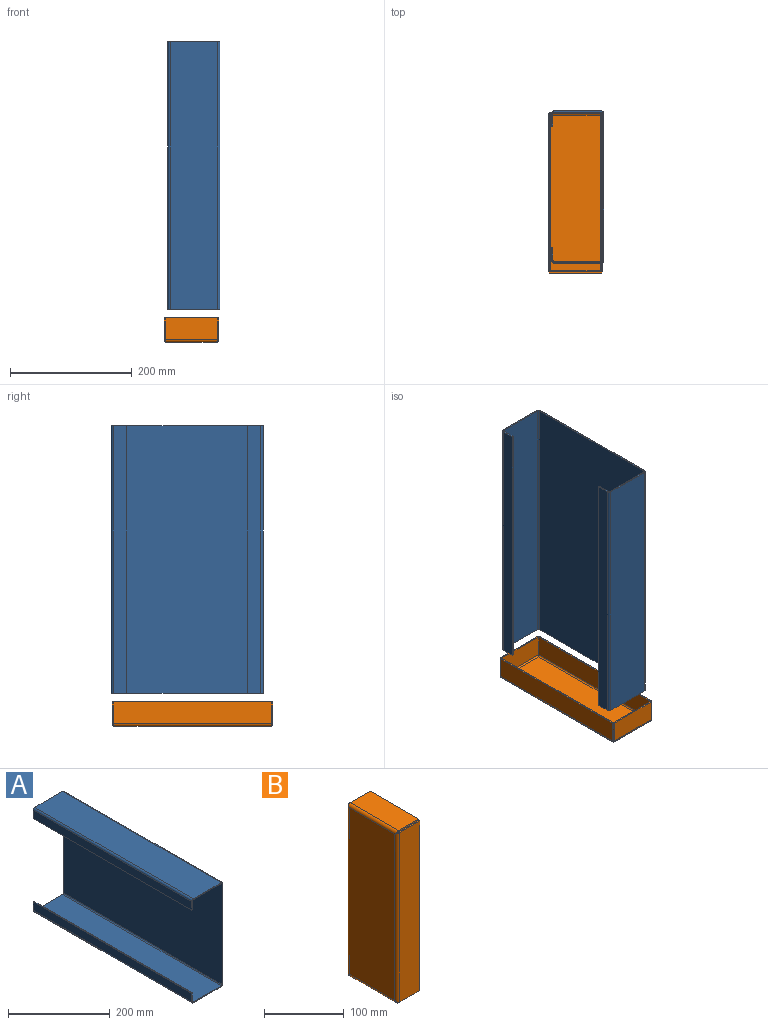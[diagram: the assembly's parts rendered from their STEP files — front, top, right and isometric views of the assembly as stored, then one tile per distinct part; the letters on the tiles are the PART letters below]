
ASSEMBLY  parts=2 mates=2
PART A: 38 faces, bbox 86x440x250 mm
  f0: plane 20.7x2mm, normal (0,1,0), area 41.4mm2, adj f2,f3,f4,f35
  f1: plane 20.7x2mm, normal (0,-1,0), area 41.4mm2, adj f2,f3,f4,f34
  f2: plane 440x2mm, normal (0,0,-1), area 880mm2, adj f0,f1,f3,f4
  f3: plane 440x20.7mm, normal (1,0,0), area 9108mm2, adj f0,f1,f2,f37
  f4: plane 440x20.7mm, normal (-1,0,0), area 9108mm2, adj f0,f1,f2,f36
  f5: plane 77.4x2mm, normal (0,1,0), area 154.8mm2, adj f7,f8,f31,f35
  f6: plane 77.4x2mm, normal (0,-1,0), area 154.8mm2, adj f7,f8,f30,f34
  f7: plane 440x77.4mm, normal (0,0,-1), area 34056mm2, adj f5,f6,f33,f37
  f8: plane 440x77.4mm, normal (0,0,1), area 34056mm2, adj f5,f6,f32,f36
  f9: plane 241.4x2mm, normal (0,1,0), area 482.8mm2, adj f11,f12,f27,f31
  f10: plane 241.4x2mm, normal (0,-1,0), area 482.8mm2, adj f11,f12,f26,f30
  f11: plane 440x241.4mm, normal (-1,0,0), area 106216mm2, adj f9,f10,f29,f33
  f12: plane 440x241.4mm, normal (1,0,0), area 106216mm2, adj f9,f10,f28,f32
  f13: plane 77.4x2mm, normal (0,1,0), area 154.8mm2, adj f15,f16,f23,f27
  f14: plane 77.4x2mm, normal (0,-1,0), area 154.8mm2, adj f15,f16,f22,f26
  f15: plane 440x77.4mm, normal (0,0,1), area 34056mm2, adj f13,f14,f25,f29
  f16: plane 440x77.4mm, normal (0,0,-1), area 34056mm2, adj f13,f14,f24,f28
  f17: plane 20.7x2mm, normal (0,1,0), area 41.4mm2, adj f18,f20,f21,f23
  f18: plane 440x2mm, normal (0,0,1), area 880mm2, adj f17,f19,f20,f21
  f19: plane 20.7x2mm, normal (0,-1,0), area 41.4mm2, adj f18,f20,f21,f22
  f20: plane 440x20.7mm, normal (1,0,0), area 9108mm2, adj f17,f18,f19,f25
  f21: plane 440x20.7mm, normal (-1,0,0), area 9108mm2, adj f17,f18,f19,f24
  f22: plane 4.3x4.3mm, normal (0,-1,0), area 10.4mm2, adj f14,f19,f24,f25
  f23: plane 4.3x4.3mm, normal (0,1,0), area 10.4mm2, adj f13,f17,f24,f25
  f24: cylinder r=4.3mm len=440mm, axis (0,-1,0), area 2971.9mm2, adj f16,f21,f22,f23
  f25: cylinder r=2.3mm len=440mm, axis (0,-1,0), area 1589.6mm2, adj f15,f20,f22,f23
  f26: plane 4.3x4.3mm, normal (0,-1,0), area 10.4mm2, adj f10,f14,f28,f29
  f27: plane 4.3x4.3mm, normal (0,1,0), area 10.4mm2, adj f9,f13,f28,f29
  f28: cylinder r=4.3mm len=440mm, axis (0,-1,0), area 2971.9mm2, adj f12,f16,f26,f27
  f29: cylinder r=2.3mm len=440mm, axis (0,-1,0), area 1589.6mm2, adj f11,f15,f26,f27
  f30: plane 4.3x4.3mm, normal (0,-1,0), area 10.4mm2, adj f6,f10,f32,f33
  f31: plane 4.3x4.3mm, normal (0,1,0), area 10.4mm2, adj f5,f9,f32,f33
  f32: cylinder r=4.3mm len=440mm, axis (0,-1,0), area 2971.9mm2, adj f8,f12,f30,f31
  f33: cylinder r=2.3mm len=440mm, axis (0,-1,0), area 1589.6mm2, adj f7,f11,f30,f31
  f34: plane 4.3x4.3mm, normal (0,-1,0), area 10.4mm2, adj f1,f6,f36,f37
  f35: plane 4.3x4.3mm, normal (0,1,0), area 10.4mm2, adj f0,f5,f36,f37
  f36: cylinder r=4.3mm len=440mm, axis (0,-1,0), area 2971.9mm2, adj f4,f8,f34,f35
  f37: cylinder r=2.3mm len=440mm, axis (0,-1,0), area 1589.6mm2, adj f3,f7,f34,f35
PART B: 42 faces, bbox 40x90x264 mm
  f0: plane 255.4x81.4mm, normal (-1,0,0), area 20789.6mm2, adj f2,f3,f4,f5,f13,f22,f31,f40
  f1: plane 255.4x81.4mm, normal (1,0,0), area 20789.6mm2, adj f2,f3,f4,f5,f14,f23,f32,f41
  f2: plane 2x0.01mm, normal (0,-0.71,0.71), area 0mm2, adj f0,f1,f21,f29
  f3: plane 2x0.01mm, normal (0,0.71,0.71), area 0mm2, adj f0,f1,f20,f38
  f4: plane 2x0.01mm, normal (0,0.71,-0.71), area 0mm2, adj f0,f1,f11,f39
  f5: plane 2x0.01mm, normal (0,-0.71,-0.71), area 0mm2, adj f0,f1,f12,f30
  f6: plane 85.96x2mm, normal (1,0,0), area 171.9mm2, adj f7,f8,f9,f10
  f7: plane 35.7x2mm, normal (0,-1,0), area 71.4mm2, adj f6,f9,f10,f12
  f8: plane 35.7x2mm, normal (0,1,0), area 71.4mm2, adj f6,f9,f10,f11
  f9: plane 85.96x35.7mm, normal (0,0,-1), area 3068.8mm2, adj f6,f7,f8,f13
  f10: plane 85.96x35.7mm, normal (0,0,1), area 3068.8mm2, adj f6,f7,f8,f14
  f11: bspline ~4.3x4.3mm, area 11.6mm2, adj f4,f8,f13,f14
  f12: bspline ~4.3x4.3mm, area 11.5mm2, adj f5,f7,f13,f14
  f13: cylinder r=4.3mm len=85.96mm, axis (0,1,0), area 569.4mm2, adj f0,f9,f11,f12
  f14: cylinder r=2.3mm len=85.96mm, axis (0,1,0), area 304.6mm2, adj f1,f10,f11,f12
  f15: plane 85.96x2mm, normal (1,0,0), area 171.9mm2, adj f16,f17,f18,f19
  f16: plane 35.7x2mm, normal (0,1,0), area 71.4mm2, adj f15,f18,f19,f20
  f17: plane 35.7x2mm, normal (0,-1,0), area 71.4mm2, adj f15,f18,f19,f21
  f18: plane 85.96x35.7mm, normal (0,0,1), area 3068.8mm2, adj f15,f16,f17,f22
  f19: plane 85.96x35.7mm, normal (0,0,-1), area 3068.8mm2, adj f15,f16,f17,f23
  f20: bspline ~4.3x4.3mm, area 11.5mm2, adj f3,f16,f22,f23
  f21: bspline ~4.3x4.3mm, area 11.6mm2, adj f2,f17,f22,f23
  f22: cylinder r=4.3mm len=85.96mm, axis (0,1,0), area 569.4mm2, adj f0,f18,f20,f21
  f23: cylinder r=2.3mm len=85.96mm, axis (0,1,0), area 304.5mm2, adj f1,f19,f20,f21
  f24: plane 259.96x2mm, normal (1,0,0), area 519.9mm2, adj f25,f26,f27,f28
  f25: plane 35.7x2mm, normal (0,0,1), area 71.4mm2, adj f24,f27,f28,f29
  f26: plane 35.7x2mm, normal (0,0,-1), area 71.4mm2, adj f24,f27,f28,f30
  f27: plane 259.96x35.7mm, normal (0,-1,0), area 9280.6mm2, adj f24,f25,f26,f31
  f28: plane 259.96x35.7mm, normal (0,1,0), area 9280.6mm2, adj f24,f25,f26,f32
  f29: bspline ~4.3x4.3mm, area 11.5mm2, adj f2,f25,f31,f32
  f30: bspline ~4.3x4.3mm, area 11.6mm2, adj f5,f26,f31,f32
  f31: cylinder r=4.3mm len=259.96mm, axis (0,0,1), area 1744.6mm2, adj f0,f27,f29,f30
  f32: cylinder r=2.3mm len=259.96mm, axis (0,0,1), area 933.2mm2, adj f1,f28,f29,f30
  f33: plane 259.96x2mm, normal (1,0,0), area 519.9mm2, adj f34,f35,f36,f37
  f34: plane 35.7x2mm, normal (0,0,-1), area 71.4mm2, adj f33,f36,f37,f39
  f35: plane 35.7x2mm, normal (0,0,1), area 71.4mm2, adj f33,f36,f37,f38
  f36: plane 259.96x35.7mm, normal (0,1,0), area 9280.6mm2, adj f33,f34,f35,f40
  f37: plane 259.96x35.7mm, normal (0,-1,0), area 9280.6mm2, adj f33,f34,f35,f41
  f38: bspline ~4.3x4.3mm, area 11.6mm2, adj f3,f35,f40,f41
  f39: bspline ~4.3x4.3mm, area 11.5mm2, adj f4,f34,f40,f41
  f40: cylinder r=4.3mm len=259.96mm, axis (0,0,1), area 1744.6mm2, adj f0,f36,f38,f39
  f41: cylinder r=2.3mm len=259.96mm, axis (0,0,1), area 933.2mm2, adj f1,f37,f38,f39
PLACE A rot(axis=(-1,0,0),90deg) t=(-55.89,-93.73,-222)mm fixed
PLACE B rot(axis=(-0.58,-0.58,-0.58),120deg) t=(-145.89,-357.73,-276.05)mm
MATE planar B.f36 <-> A.f11  axis (1,0,0) through (-57.89,-227.73,-253.9)mm
MATE planar B.f18 <-> A.f7  axis (0,1,0) through (-102.89,-95.73,-253.9)mm
